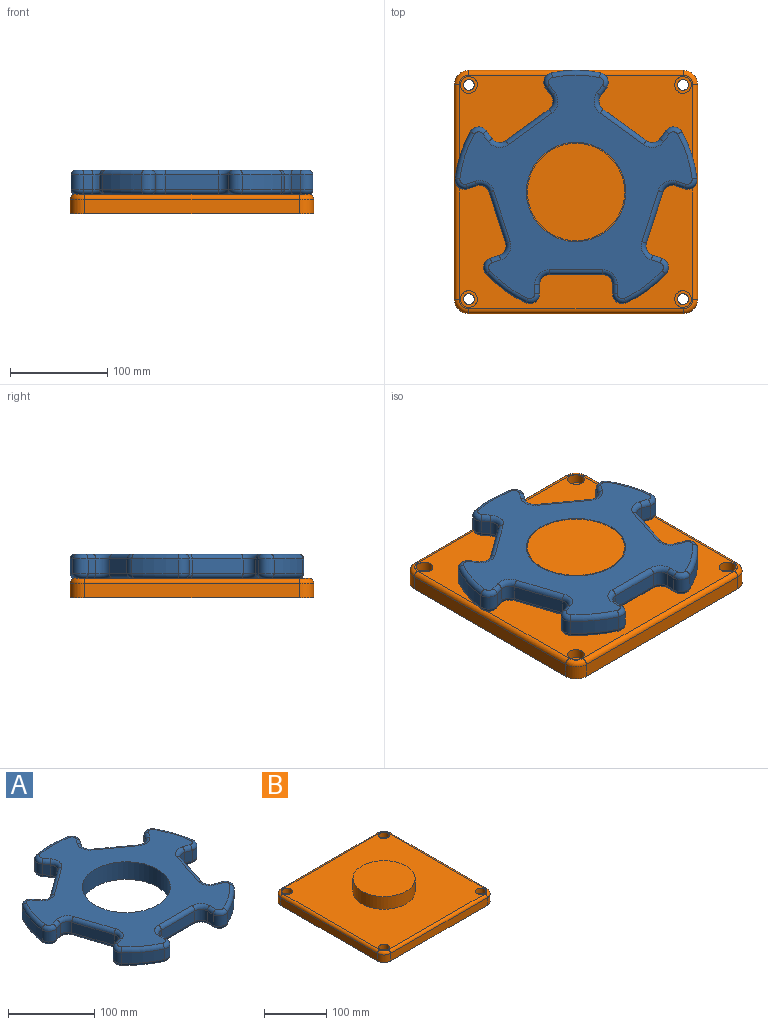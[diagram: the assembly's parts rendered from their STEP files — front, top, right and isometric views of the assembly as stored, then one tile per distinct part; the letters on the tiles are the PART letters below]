
ASSEMBLY  parts=2 mates=1
PART A: 123 faces, bbox 268.9x258.5x25 mm
  f0: plane 238.57x229.73mm, normal (0,0,1), area 21505.7mm2, adj f6,f43,f44,f45,f46,f47,f48,f49
  f1: plane 238.57x229.73mm, normal (0,0,-1), area 21505.7mm2, adj f6,f83,f84,f85,f86,f87,f88,f89
  f2: cylinder r=125mm len=40.68mm, axis (0,0,-1), area 759.5mm2, adj f13,f42,f51,f91
  f3: cylinder r=125mm len=47.82mm, axis (0,0,-1), area 759.5mm2, adj f35,f41,f67,f107
  f4: cylinder r=125mm len=50.29mm, axis (0,0,-1), area 759.5mm2, adj f28,f34,f82,f122
  f5: cylinder r=125mm len=47.82mm, axis (0,0,-1), area 759.5mm2, adj f21,f27,f66,f106
  f6: cylinder r=51mm len=102mm, axis (0,0,-1), area 8011.1mm2, adj f0,f1
  f7: cylinder r=125mm len=40.68mm, axis (0,0,-1), area 759.5mm2, adj f14,f20,f50,f90
  f8: plane 15x9.73mm, normal (-1,0,0), area 146mm2, adj f11,f14,f46,f86
  f9: plane 55x15mm, normal (0,-1,0), area 825mm2, adj f11,f12,f43,f83
  f10: plane 15x9.73mm, normal (1,0,0), area 146mm2, adj f12,f13,f47,f87
  f11: cylinder r=10mm len=15mm, axis (0,0,-1), area 235.6mm2, adj f8,f9,f44,f84
  f12: cylinder r=10mm len=15mm, axis (0,0,-1), area 235.6mm2, adj f9,f10,f45,f85
  f13: cylinder r=10mm len=15mm, axis (0,0,-1), area 299.5mm2, adj f2,f10,f49,f89
  f14: cylinder r=10mm len=15mm, axis (0,0,-1), area 299.5mm2, adj f7,f8,f48,f88
  f15: plane 15x9.26mm, normal (-0.31,-0.95,0), area 146mm2, adj f18,f21,f62,f102
  f16: plane 52.31x17mm, normal (0.95,-0.31,0), area 825mm2, adj f18,f19,f58,f98
  f17: plane 15x9.26mm, normal (0.31,0.95,0), area 146mm2, adj f19,f20,f54,f94
  f18: cylinder r=10mm len=15mm, axis (0,0,-1), area 235.6mm2, adj f15,f16,f60,f100
  f19: cylinder r=10mm len=15mm, axis (0,0,-1), area 235.6mm2, adj f16,f17,f56,f96
  f20: cylinder r=10mm len=16.25mm, axis (0,0,-1), area 299.5mm2, adj f7,f17,f52,f92
  f21: cylinder r=10mm len=15mm, axis (0,0,-1), area 299.5mm2, adj f5,f15,f64,f104
  f22: plane 15x7.87mm, normal (0.81,-0.59,0), area 146mm2, adj f25,f28,f78,f118
  f23: plane 44.5x32.33mm, normal (0.59,0.81,0), area 825mm2, adj f25,f26,f74,f114
  f24: plane 15x7.87mm, normal (-0.81,0.59,0), area 146mm2, adj f26,f27,f70,f110
  f25: cylinder r=10mm len=15mm, axis (0,0,-1), area 235.6mm2, adj f22,f23,f76,f116
  f26: cylinder r=10mm len=15mm, axis (0,0,-1), area 235.6mm2, adj f23,f24,f72,f112
  f27: cylinder r=10mm len=16.78mm, axis (0,0,-1), area 299.5mm2, adj f5,f24,f68,f108
  f28: cylinder r=10mm len=15.67mm, axis (0,0,-1), area 299.5mm2, adj f4,f22,f80,f120
  f29: plane 15x7.87mm, normal (0.81,0.59,0), area 146mm2, adj f32,f35,f71,f111
  f30: plane 44.5x32.33mm, normal (-0.59,0.81,0), area 825mm2, adj f32,f33,f75,f115
  f31: plane 15x7.87mm, normal (-0.81,-0.59,0), area 146mm2, adj f33,f34,f79,f119
  f32: cylinder r=10mm len=15mm, axis (0,0,-1), area 235.6mm2, adj f29,f30,f73,f113
  f33: cylinder r=10mm len=15mm, axis (0,0,-1), area 235.6mm2, adj f30,f31,f77,f117
  f34: cylinder r=10mm len=15.67mm, axis (0,0,-1), area 299.5mm2, adj f4,f31,f81,f121
  f35: cylinder r=10mm len=16.78mm, axis (0,0,-1), area 299.5mm2, adj f3,f29,f69,f109
  f36: plane 15x9.26mm, normal (-0.31,0.95,0), area 146mm2, adj f39,f42,f55,f95
  f37: plane 52.31x17mm, normal (-0.95,-0.31,0), area 825mm2, adj f39,f40,f59,f99
  f38: plane 15x9.26mm, normal (0.31,-0.95,0), area 146mm2, adj f40,f41,f63,f103
  f39: cylinder r=10mm len=15mm, axis (0,0,-1), area 235.6mm2, adj f36,f37,f57,f97
  f40: cylinder r=10mm len=15mm, axis (0,0,-1), area 235.6mm2, adj f37,f38,f61,f101
  f41: cylinder r=10mm len=15mm, axis (0,0,-1), area 299.5mm2, adj f3,f38,f65,f105
  f42: cylinder r=10mm len=16.25mm, axis (0,0,-1), area 299.5mm2, adj f2,f36,f53,f93
  f43: cylinder r=5mm len=55mm, axis (1,0,0), area 432mm2, adj f0,f9,f44,f45
  f44: torus R=15mm, axis (0,0,1), area 145.8mm2, adj f0,f11,f43,f46
  f45: torus R=15mm, axis (0,0,1), area 145.8mm2, adj f0,f12,f43,f47
  f46: cylinder r=5mm len=9.73mm, axis (0,-1,0), area 76.4mm2, adj f0,f8,f44,f48
  f47: cylinder r=5mm len=9.73mm, axis (0,1,0), area 76.4mm2, adj f0,f10,f45,f49
  f48: torus R=5mm, axis (0,0,1), area 128.3mm2, adj f0,f14,f46,f50
  f49: torus R=5mm, axis (0,0,1), area 128.3mm2, adj f0,f13,f47,f51
  f50: torus R=120mm, axis (0,0,1), area 391.9mm2, adj f0,f7,f48,f52
  f51: torus R=120mm, axis (0,0,1), area 391.9mm2, adj f0,f2,f49,f53
  f52: torus R=5mm, axis (0,0,1), area 128.3mm2, adj f0,f20,f50,f54
  f53: torus R=5mm, axis (0,0,1), area 128.3mm2, adj f0,f42,f51,f55
  f54: cylinder r=5mm len=10.8mm, axis (-0.95,0.31,0), area 76.4mm2, adj f0,f17,f52,f56
  f55: cylinder r=5mm len=10.8mm, axis (-0.95,-0.31,0), area 76.4mm2, adj f0,f36,f53,f57
  f56: torus R=15mm, axis (0,0,1), area 145.8mm2, adj f0,f19,f54,f58
  f57: torus R=15mm, axis (0,0,1), area 145.8mm2, adj f0,f39,f55,f59
  f58: cylinder r=5mm len=53.85mm, axis (0.31,0.95,0), area 432mm2, adj f0,f16,f56,f60
  f59: cylinder r=5mm len=53.85mm, axis (0.31,-0.95,0), area 432mm2, adj f0,f37,f57,f61
  f60: torus R=15mm, axis (0,0,1), area 145.8mm2, adj f0,f18,f58,f62
  f61: torus R=15mm, axis (0,0,1), area 145.8mm2, adj f0,f40,f59,f63
  f62: cylinder r=5mm len=10.8mm, axis (0.95,-0.31,0), area 76.4mm2, adj f0,f15,f60,f64
  f63: cylinder r=5mm len=10.8mm, axis (0.95,0.31,0), area 76.4mm2, adj f0,f38,f61,f65
  f64: torus R=5mm, axis (0,0,1), area 128.3mm2, adj f0,f21,f62,f66
  f65: torus R=5mm, axis (0,0,1), area 128.3mm2, adj f0,f41,f63,f67
  f66: torus R=120mm, axis (0,0,1), area 391.9mm2, adj f0,f5,f64,f68
  f67: torus R=120mm, axis (0,0,1), area 391.9mm2, adj f0,f3,f65,f69
  f68: torus R=5mm, axis (0,0,1), area 128.3mm2, adj f0,f27,f66,f70
  f69: torus R=5mm, axis (0,0,1), area 128.3mm2, adj f0,f35,f67,f71
  f70: cylinder r=5mm len=10.81mm, axis (-0.59,-0.81,0), area 76.4mm2, adj f0,f24,f68,f72
  f71: cylinder r=5mm len=10.81mm, axis (-0.59,0.81,0), area 76.4mm2, adj f0,f29,f69,f73
  f72: torus R=15mm, axis (0,0,1), area 145.8mm2, adj f0,f26,f70,f74
  f73: torus R=15mm, axis (0,0,1), area 145.8mm2, adj f0,f32,f71,f75
  f74: cylinder r=5mm len=47.44mm, axis (-0.81,0.59,0), area 432mm2, adj f0,f23,f72,f76
  f75: cylinder r=5mm len=47.44mm, axis (-0.81,-0.59,0), area 432mm2, adj f0,f30,f73,f77
  f76: torus R=15mm, axis (0,0,1), area 145.8mm2, adj f0,f25,f74,f78
  f77: torus R=15mm, axis (0,0,1), area 145.8mm2, adj f0,f33,f75,f79
  f78: cylinder r=5mm len=10.81mm, axis (0.59,0.81,0), area 76.4mm2, adj f0,f22,f76,f80
  f79: cylinder r=5mm len=10.81mm, axis (0.59,-0.81,0), area 76.4mm2, adj f0,f31,f77,f81
  f80: torus R=5mm, axis (0,0,1), area 128.3mm2, adj f0,f28,f78,f82
  f81: torus R=5mm, axis (0,0,1), area 128.3mm2, adj f0,f34,f79,f82
  f82: torus R=120mm, axis (0,0,1), area 391.9mm2, adj f0,f4,f80,f81
  f83: cylinder r=5mm len=55mm, axis (-1,0,0), area 432mm2, adj f1,f9,f84,f85
  f84: torus R=15mm, axis (0,0,1), area 145.8mm2, adj f1,f11,f83,f86
  f85: torus R=15mm, axis (0,0,1), area 145.8mm2, adj f1,f12,f83,f87
  f86: cylinder r=5mm len=9.73mm, axis (0,1,0), area 76.4mm2, adj f1,f8,f84,f88
  f87: cylinder r=5mm len=9.73mm, axis (0,-1,0), area 76.4mm2, adj f1,f10,f85,f89
  f88: torus R=5mm, axis (0,0,1), area 128.3mm2, adj f1,f14,f86,f90
  f89: torus R=5mm, axis (0,0,1), area 128.3mm2, adj f1,f13,f87,f91
  f90: torus R=120mm, axis (0,0,1), area 391.9mm2, adj f1,f7,f88,f92
  f91: torus R=120mm, axis (0,0,1), area 391.9mm2, adj f1,f2,f89,f93
  f92: torus R=5mm, axis (0,0,1), area 128.3mm2, adj f1,f20,f90,f94
  f93: torus R=5mm, axis (0,0,1), area 128.3mm2, adj f1,f42,f91,f95
  f94: cylinder r=5mm len=10.8mm, axis (0.95,-0.31,0), area 76.4mm2, adj f1,f17,f92,f96
  f95: cylinder r=5mm len=10.8mm, axis (0.95,0.31,0), area 76.4mm2, adj f1,f36,f93,f97
  f96: torus R=15mm, axis (0,0,1), area 145.8mm2, adj f1,f19,f94,f98
  f97: torus R=15mm, axis (0,0,1), area 145.8mm2, adj f1,f39,f95,f99
  f98: cylinder r=5mm len=53.85mm, axis (-0.31,-0.95,0), area 432mm2, adj f1,f16,f96,f100
  f99: cylinder r=5mm len=53.85mm, axis (-0.31,0.95,0), area 432mm2, adj f1,f37,f97,f101
  f100: torus R=15mm, axis (0,0,1), area 145.8mm2, adj f1,f18,f98,f102
  f101: torus R=15mm, axis (0,0,1), area 145.8mm2, adj f1,f40,f99,f103
  f102: cylinder r=5mm len=10.8mm, axis (-0.95,0.31,0), area 76.4mm2, adj f1,f15,f100,f104
  f103: cylinder r=5mm len=10.8mm, axis (-0.95,-0.31,0), area 76.4mm2, adj f1,f38,f101,f105
  f104: torus R=5mm, axis (0,0,1), area 128.3mm2, adj f1,f21,f102,f106
  f105: torus R=5mm, axis (0,0,1), area 128.3mm2, adj f1,f41,f103,f107
  f106: torus R=120mm, axis (0,0,1), area 391.9mm2, adj f1,f5,f104,f108
  f107: torus R=120mm, axis (0,0,1), area 391.9mm2, adj f1,f3,f105,f109
  f108: torus R=5mm, axis (0,0,1), area 128.3mm2, adj f1,f27,f106,f110
  f109: torus R=5mm, axis (0,0,1), area 128.3mm2, adj f1,f35,f107,f111
  f110: cylinder r=5mm len=10.81mm, axis (0.59,0.81,0), area 76.4mm2, adj f1,f24,f108,f112
  f111: cylinder r=5mm len=10.81mm, axis (0.59,-0.81,0), area 76.4mm2, adj f1,f29,f109,f113
  f112: torus R=15mm, axis (0,0,1), area 145.8mm2, adj f1,f26,f110,f114
  f113: torus R=15mm, axis (0,0,1), area 145.8mm2, adj f1,f32,f111,f115
  f114: cylinder r=5mm len=47.44mm, axis (0.81,-0.59,0), area 432mm2, adj f1,f23,f112,f116
  f115: cylinder r=5mm len=47.44mm, axis (0.81,0.59,0), area 432mm2, adj f1,f30,f113,f117
  f116: torus R=15mm, axis (0,0,1), area 145.8mm2, adj f1,f25,f114,f118
  f117: torus R=15mm, axis (0,0,1), area 145.8mm2, adj f1,f33,f115,f119
  f118: cylinder r=5mm len=10.81mm, axis (-0.59,-0.81,0), area 76.4mm2, adj f1,f22,f116,f120
  f119: cylinder r=5mm len=10.81mm, axis (-0.59,0.81,0), area 76.4mm2, adj f1,f31,f117,f121
  f120: torus R=5mm, axis (0,0,1), area 128.3mm2, adj f1,f28,f118,f122
  f121: torus R=5mm, axis (0,0,1), area 128.3mm2, adj f1,f34,f119,f122
  f122: torus R=120mm, axis (0,0,1), area 391.9mm2, adj f1,f4,f120,f121
PART B: 32 faces, bbox 252.5x252.5x45 mm
  f0: plane 220x15mm, normal (1,0,0), area 3300mm2, adj f5,f8,f11,f27
  f1: plane 220x15mm, normal (0,1,0), area 3300mm2, adj f5,f8,f9,f31
  f2: plane 220x15mm, normal (-1,0,0), area 3300mm2, adj f5,f9,f10,f28
  f3: plane 220x15mm, normal (0,-1,0), area 3300mm2, adj f5,f10,f11,f24
  f4: plane 240x240mm, normal (0,0,1), area 48725.4mm2, adj f6,f14,f17,f20,f23,f24,f25,f26
  f5: plane 250x250mm, normal (0,0,-1), area 61926.7mm2, adj f0,f1,f2,f3,f8,f9,f10,f11
  f6: cylinder r=50mm len=100mm, axis (0,0,-1), area 7854mm2, adj f4,f7
  f7: plane 100x100mm, normal (0,0,1), area 7854mm2, adj f6
  f8: cylinder r=15mm len=15mm, axis (0,0,-1), area 353.4mm2, adj f0,f1,f5,f29
  f9: cylinder r=15mm len=15mm, axis (0,0,1), area 353.4mm2, adj f1,f2,f5,f30
  f10: cylinder r=15mm len=15mm, axis (0,0,-1), area 353.4mm2, adj f2,f3,f5,f26
  f11: cylinder r=15mm len=15mm, axis (0,0,1), area 353.4mm2, adj f0,f3,f5,f25
  f12: cylinder r=5.5mm len=11mm, axis (0,0,1), area 345.6mm2, adj f5,f13
  f13: plane 17.25x17.25mm, normal (0,0,1), area 138.7mm2, adj f12,f14
  f14: cylinder r=8.62mm len=17.25mm, axis (0,0,1), area 541.9mm2, adj f4,f13
  f15: cylinder r=5.5mm len=11mm, axis (0,0,1), area 345.6mm2, adj f5,f16
  f16: plane 17.25x17.25mm, normal (0,0,1), area 138.7mm2, adj f15,f17
  f17: cylinder r=8.62mm len=17.25mm, axis (0,0,1), area 541.9mm2, adj f4,f16
  f18: cylinder r=5.5mm len=11mm, axis (0,0,1), area 345.6mm2, adj f5,f19
  f19: plane 17.25x17.25mm, normal (0,0,1), area 138.7mm2, adj f18,f20
  f20: cylinder r=8.62mm len=17.25mm, axis (0,0,1), area 541.9mm2, adj f4,f19
  f21: cylinder r=5.5mm len=11mm, axis (0,0,1), area 345.6mm2, adj f5,f22
  f22: plane 17.25x17.25mm, normal (0,0,1), area 138.7mm2, adj f21,f23
  f23: cylinder r=8.62mm len=17.25mm, axis (0,0,1), area 541.9mm2, adj f4,f22
  f24: cylinder r=5mm len=220mm, axis (-1,0,0), area 1727.9mm2, adj f3,f4,f25,f26
  f25: torus R=10mm, axis (0,0,1), area 162.6mm2, adj f4,f11,f24,f27
  f26: torus R=10mm, axis (0,0,1), area 162.6mm2, adj f4,f10,f24,f28
  f27: cylinder r=5mm len=220mm, axis (0,-1,0), area 1727.9mm2, adj f0,f4,f25,f29
  f28: cylinder r=5mm len=220mm, axis (0,1,0), area 1727.9mm2, adj f2,f4,f26,f30
  f29: torus R=10mm, axis (0,0,1), area 162.6mm2, adj f4,f8,f27,f31
  f30: torus R=10mm, axis (0,0,1), area 162.6mm2, adj f4,f9,f28,f31
  f31: cylinder r=5mm len=220mm, axis (1,0,0), area 1727.9mm2, adj f1,f4,f29,f30
PLACE A at identity
PLACE B at identity fixed
MATE revolute A.f2 <-> B.f6  axis (0,0,-1) through (0,0,32.5)mm
